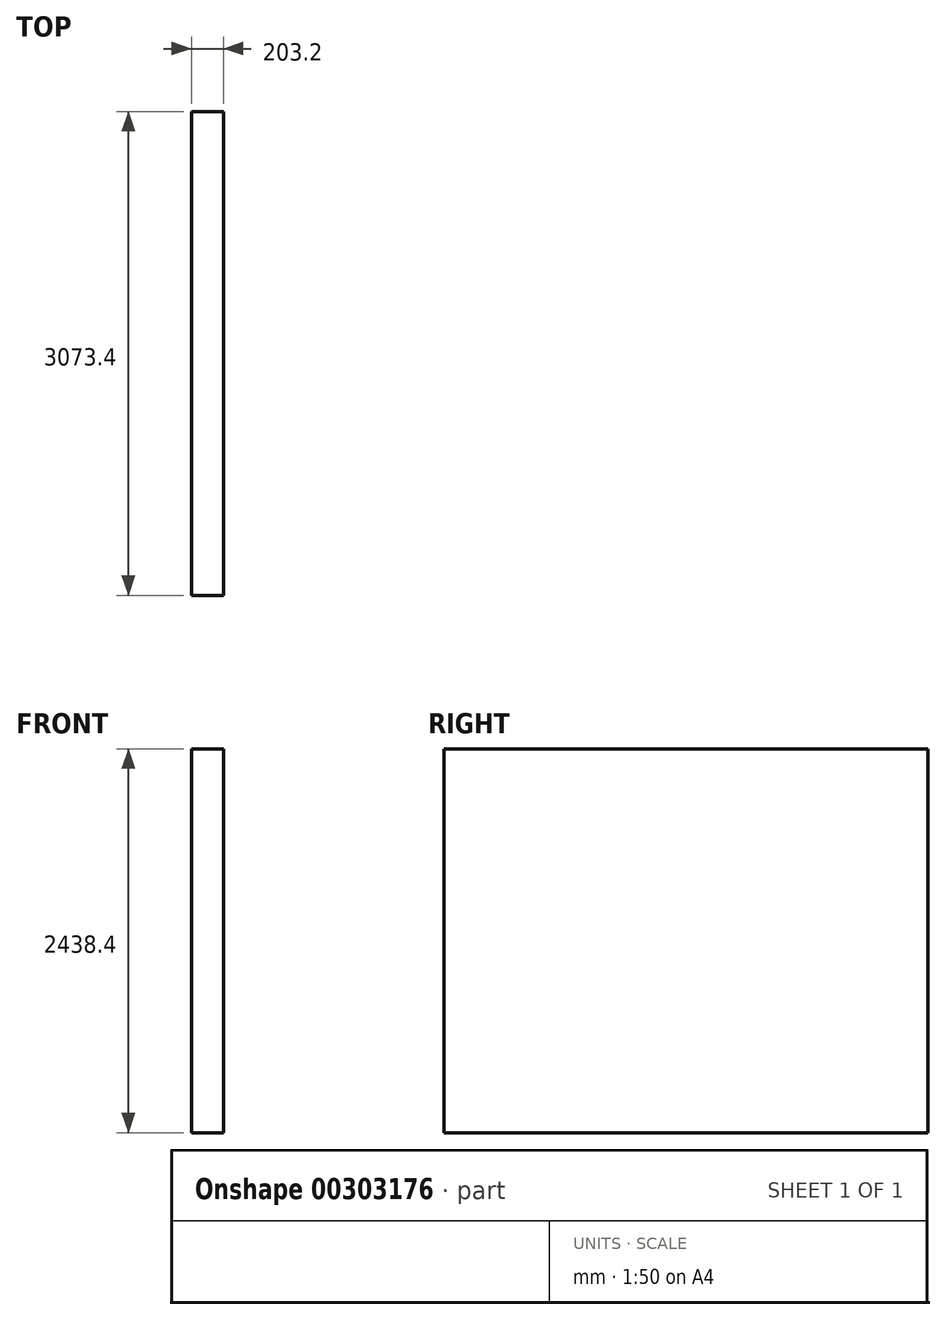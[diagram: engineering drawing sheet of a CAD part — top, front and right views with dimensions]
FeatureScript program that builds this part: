
annotation { "Feature Type Name" : "Feature", "Feature Type Description" : "" }
export const myFeature = defineFeature(function(context is Context, id is Id, definition is map)
    precondition{}
    {
        {
            var Q0;
            Q0=qCreatedBy(makeId("Top.planeOp"),FACE);
            var sketch = newSketch(context, id + "F1", { "sketchPlane" : qUnion([Q0])});
            skLineSegment(sketch, "E0.bottom", {"start": v(101.6, 1536.7) * mm, "end": v(-101.6, 1536.7) * mm});
            skLineSegment(sketch, "E0.top", {"start": v(101.6, -1536.7) * mm, "end": v(-101.6, -1536.7) * mm});
            skLineSegment(sketch, "E0.left", {"start": v(101.6, 1536.7) * mm, "end": v(101.6, -1536.7) * mm});
            skLineSegment(sketch, "E0.right", {"start": v(-101.6, 1536.7) * mm, "end": v(-101.6, -1536.7) * mm});
            skPoint(sketch, "E0.middle", {"position": v(0, 0) * mm});
            skSolve(sketch);
        }
        {
            var Q0;
            Q0=makeQuery(id+"F1.imprint","IMPRINT",FACE,{"disambiguationData":[TD([[makeQuery(id+"F1.imprint","IMPRINT",EDGE,{"derivedFrom":sQuery(id+"F1.wireOp",EDGE,"E0.bottom")}),1.0]])]});
            extrude(context, id + "F0", {"entities" : qUnion([Q0]), "depth" : 2438.4 * mm});
        }
    });
